# Revit family: HARPER Shower Channel Waste 900mm - RFA 2
name_source: partatom
category: Generic Models
units: mm (PartAtom-declared; Revit-internal decimal feet)

## family parameters
Always vertical = Yes
Can host rebar = No
Cut with Voids When Loaded = No
Maintain Annotation Orientation = No
OmniClass Number = 23.45.55.21
OmniClass Title = Drains (Wastes)
Part Type = Normal
Room Calculation Point = No
Round Connector Dimension = Use Diameter
Shared = No
Work Plane-Based = No

## types (1)
- HARPER Shower Channel Waste 900mm
    CW Connection = False
    Default Elevation = 0 mm  [stored 0 ft]
    Description = HARPER Shower Channel Waste 900mm
    HW Connection = False
    Manufacturer = ABI Interiors PTY LTD
    Model = Brass (10458), Copper (10231), Gunmetal (10230), Stainless Steel (10232)
    URL = https://www.abiinteriors.com.au
    Vent Connection = False
    Waste Connection = False

note: [stored X ft] marks values corroborated as IEEE doubles in the binary element streams (Revit-internal decimal feet)

## geometry (parser evidence)
native form markers: Sweep x3
no freeform markers — native parametric forms only
